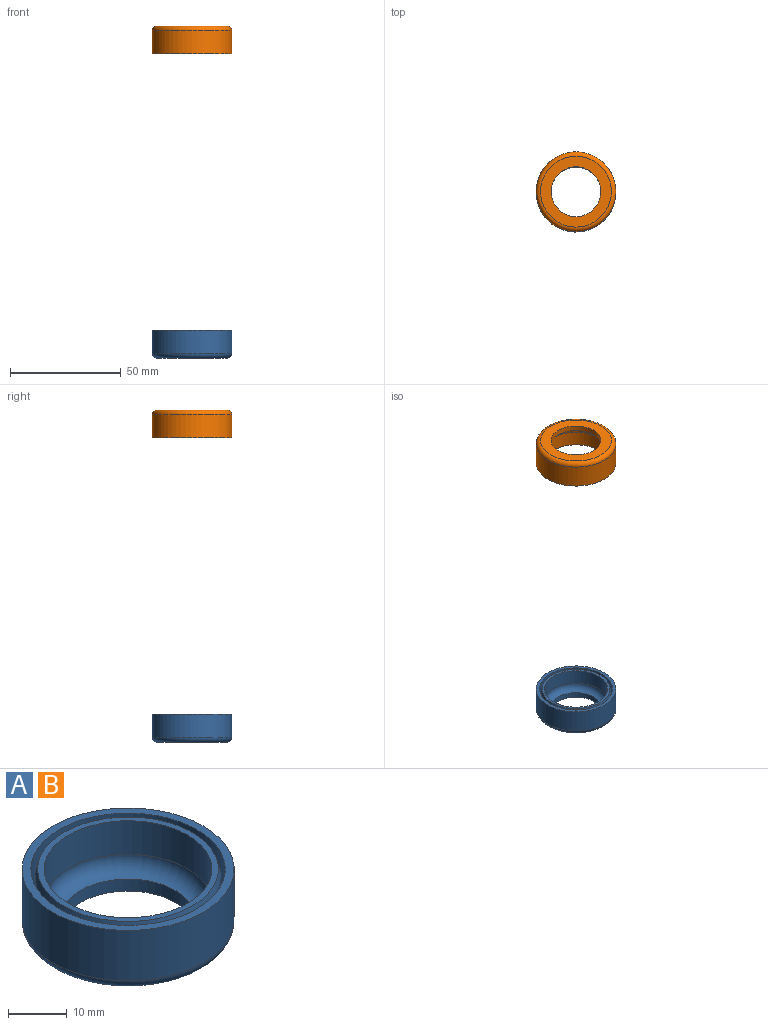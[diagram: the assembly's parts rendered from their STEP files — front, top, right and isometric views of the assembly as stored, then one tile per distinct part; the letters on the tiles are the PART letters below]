
ASSEMBLY  parts=2 mates=2
PART A: 12 faces, bbox 39x39x12.5 mm
  f0: plane 32x32mm, normal (0,0,-1), area 406.6mm2, adj f1,f11
  f1: cylinder r=11.25mm len=22.5mm, axis (0,0,1), area 176.7mm2, adj f0,f2
  f2: torus R=11.25mm, axis (0,0,1), area 389.6mm2, adj f1,f3
  f3: cylinder r=14.25mm len=28.5mm, axis (0,0,1), area 626.7mm2, adj f2,f4
  f4: plane 30.7x30.7mm, normal (0,0,1), area 102.3mm2, adj f3,f10
  f5: cylinder r=15.75mm len=31.5mm, axis (0,0,1), area 841.9mm2, adj f6,f10
  f6: plane 33x33mm, normal (0,0,1), area 76mm2, adj f5,f7
  f7: cylinder r=16.5mm len=33mm, axis (0,0,1), area 1036.7mm2, adj f6,f8
  f8: plane 36x36mm, normal (0,0,1), area 162.6mm2, adj f7,f9
  f9: cylinder r=18mm len=36mm, axis (0,0,1), area 1187.5mm2, adj f8,f11
  f10: cone r=15.35mm half-angle=15deg, axis (0,0,-1), area 151mm2, adj f4,f5
  f11: torus R=16mm, axis (0,0,1), area 341mm2, adj f0,f9
PART B: same geometry as A
PLACE A at identity fixed
PLACE B rot(axis=(0.71,-0.71,0),180deg) t=(0,0,150)mm
MATE planar B.f1 <-> A.f1  axis (0,0,1) through (0,0,150)mm
MATE cylindrical A.f1 <-> B.f1  axis (0,0,1) through (0,0,2)mm
